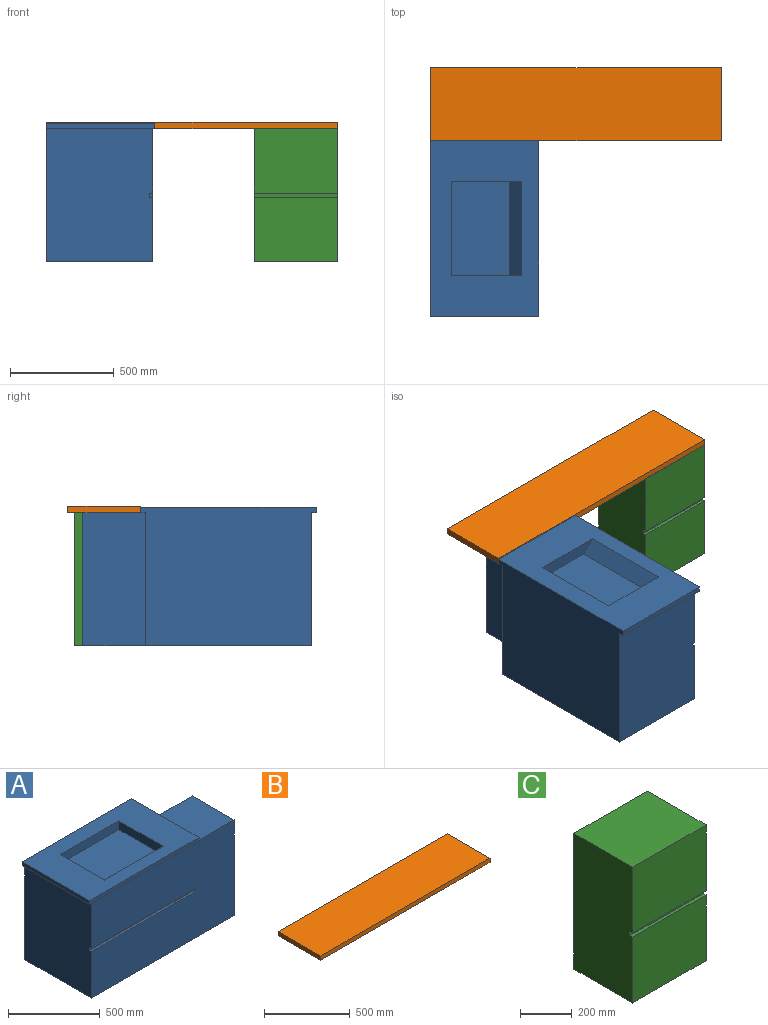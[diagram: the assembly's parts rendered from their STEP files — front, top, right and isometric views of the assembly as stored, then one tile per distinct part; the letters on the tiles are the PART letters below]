
ASSEMBLY  parts=3 mates=6
PART A: 23 faces, bbox 1122.5x520x665 mm
  f0: plane 192x22.5mm, normal (0,0,-1), area 4320mm2, adj f4,f5,f10,f21
  f1: plane 845x520mm, normal (0,0,1), area 286400mm2, adj f5,f10,f11,f12,f14,f15,f16,f18
  f2: plane 640x512mm, normal (-1,0,0), area 327380mm2, adj f3,f5,f6,f7,f8,f9,f13
  f3: plane 1100x640mm, normal (0,-1,0), area 688000mm2, adj f2,f6,f7,f8,f13,f19,f20,f22
  f4: plane 640x192mm, normal (1,0,0), area 122880mm2, adj f0,f5,f6,f21
  f5: plane 845x665mm, normal (0,1,0), area 533125mm2, adj f0,f1,f2,f4,f6,f10,f11,f13
  f6: plane 1100x512mm, normal (0,0,-1), area 505600mm2, adj f2,f3,f4,f5,f20,f21
  f7: plane 800x15mm, normal (0,0,-1), area 12000mm2, adj f2,f3,f9,f19
  f8: plane 800x15mm, normal (0,0,1), area 12000mm2, adj f2,f3,f9,f19
  f9: plane 800x20mm, normal (0,-1,0), area 16000mm2, adj f2,f7,f8,f19
  f10: plane 520x25mm, normal (1,0,0), area 13000mm2, adj f0,f1,f5,f12,f13,f22
  f11: plane 520x25mm, normal (-1,0,0), area 13000mm2, adj f1,f5,f12,f13
  f12: plane 845x25mm, normal (0,-1,0), area 21125mm2, adj f1,f10,f11,f13
  f13: plane 845x520mm, normal (0,0,-1), area 18280mm2, adj f2,f3,f5,f10,f11,f12
  f14: plane 340x60mm, normal (-1,0,0), area 18600mm2, adj f1,f15,f17,f18
  f15: plane 450x60mm, normal (0,-1,0), area 27000mm2, adj f1,f14,f16,f17
  f16: plane 340x60mm, normal (1,0,0), area 18600mm2, adj f1,f15,f17,f18
  f17: plane 450x280mm, normal (0,0,1), area 126000mm2, adj f14,f15,f16,f18
  f18: plane 450x60mm, normal (0,0.71,0.71), area 38183.8mm2, adj f1,f14,f16,f17
  f19: plane 20x15mm, normal (-1,0,0), area 300mm2, adj f3,f7,f8,f9
  f20: plane 640x320mm, normal (1,0,0), area 204800mm2, adj f3,f6,f21,f22
  f21: plane 640x300mm, normal (0,1,0), area 192000mm2, adj f0,f4,f6,f20,f22
  f22: plane 320x277.5mm, normal (0,0,1), area 88800mm2, adj f3,f10,f20,f21
PART B: 6 faces, bbox 1400x350x30 mm
  f0: plane 350x30mm, normal (-1,0,0), area 10500mm2, adj f1,f3,f4,f5
  f1: plane 1400x30mm, normal (0,-1,0), area 42000mm2, adj f0,f2,f4,f5
  f2: plane 350x30mm, normal (1,0,0), area 10500mm2, adj f1,f3,f4,f5
  f3: plane 1400x30mm, normal (0,1,0), area 42000mm2, adj f0,f2,f4,f5
  f4: plane 1400x350mm, normal (0,0,1), area 490000mm2, adj f0,f1,f2,f3
  f5: plane 1400x350mm, normal (0,0,-1), area 490000mm2, adj f0,f1,f2,f3
PART C: 10 faces, bbox 400x320x640 mm
  f0: plane 400x310mm, normal (0,-1,0), area 124000mm2, adj f1,f3,f6,f8
  f1: plane 640x320mm, normal (-1,0,0), area 204500mm2, adj f0,f2,f4,f5,f6,f7,f8,f9
  f2: plane 400x310mm, normal (0,-1,0), area 124000mm2, adj f1,f3,f5,f7
  f3: plane 640x320mm, normal (1,0,0), area 204500mm2, adj f0,f2,f4,f5,f6,f7,f8,f9
  f4: plane 640x400mm, normal (0,1,0), area 256000mm2, adj f1,f3,f5,f6
  f5: plane 400x320mm, normal (0,0,1), area 128000mm2, adj f1,f2,f3,f4
  f6: plane 400x320mm, normal (0,0,-1), area 128000mm2, adj f0,f1,f3,f4
  f7: plane 400x15mm, normal (0,0,-1), area 6000mm2, adj f1,f2,f3,f9
  f8: plane 400x15mm, normal (0,0,1), area 6000mm2, adj f0,f1,f3,f9
  f9: plane 400x20mm, normal (0,-1,0), area 8000mm2, adj f1,f3,f7,f8
PLACE A rot(axis=(0,0,1),90deg) t=(403.33,-554.36,-762.2)mm
PLACE B t=(-108.67,268.14,-122.2)mm fixed
PLACE C t=(891.33,268.14,-762.2)mm
MATE planar B.f0 <-> A.f5  axis (-1,0,0) through (-108.67,443.14,-92.2)mm
MATE planar B.f2 <-> C.f3  axis (1,0,0) through (1291.33,443.14,-107.2)mm
MATE planar A.f22 <-> B.f5  axis (0,0,1) through (243.33,406.89,-122.2)mm
MATE planar C.f5 <-> B.f5  axis (0,0,1) through (891.33,588.14,-122.2)mm
MATE planar C.f2 <-> B.f1  axis (0,-1,0) through (1091.33,268.14,-277.2)mm
MATE planar A.f10 <-> B.f1  axis (0,1,0) through (151.33,268.14,-109.7)mm
